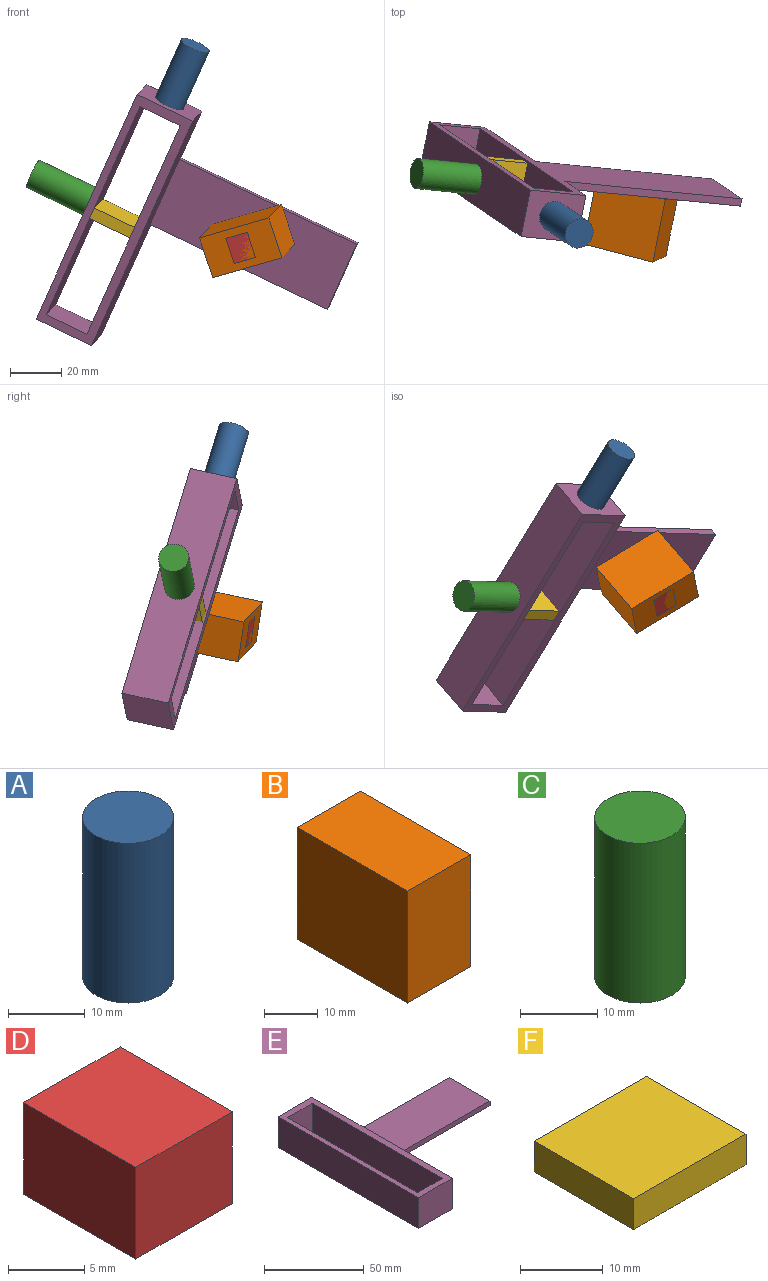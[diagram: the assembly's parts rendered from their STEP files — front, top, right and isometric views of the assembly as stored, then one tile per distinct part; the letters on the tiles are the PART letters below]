
ASSEMBLY  parts=6 mates=5
PART A: 3 faces, bbox 11.8x11.8x25.4 mm
  f0: cylinder r=5.91mm len=25.4mm, axis (0,0,-1), area 942.4mm2, adj f1,f2
  f1: plane 11.81x11.81mm, normal (0,0,1), area 109.5mm2, adj f0
  f2: plane 11.81x11.81mm, normal (0,0,-1), area 109.5mm2, adj f0
PART B: 6 faces, bbox 16.5x28.9x25.4 mm
  f0: plane 28.93x25.4mm, normal (1,0,0), area 734.7mm2, adj f1,f3,f4,f5
  f1: plane 25.4x16.52mm, normal (0,1,0), area 419.6mm2, adj f0,f2,f4,f5
  f2: plane 28.93x25.4mm, normal (-1,0,0), area 734.7mm2, adj f1,f3,f4,f5
  f3: plane 25.4x16.52mm, normal (0,-1,0), area 419.6mm2, adj f0,f2,f4,f5
  f4: plane 28.93x16.52mm, normal (0,0,1), area 477.8mm2, adj f0,f1,f2,f3
  f5: plane 28.93x16.52mm, normal (0,0,-1), area 477.8mm2, adj f0,f1,f2,f3
PART C: 3 faces, bbox 11.8x11.8x25.4 mm
  f0: cylinder r=5.88mm len=25.4mm, axis (0,0,-1), area 939mm2, adj f1,f2
  f1: plane 11.77x11.77mm, normal (0,0,1), area 108.8mm2, adj f0
  f2: plane 11.77x11.77mm, normal (0,0,-1), area 108.8mm2, adj f0
PART D: 6 faces, bbox 9x10.4x7.4 mm
  f0: plane 8.96x7.39mm, normal (0,-1,0), area 66.2mm2, adj f1,f3,f4,f5
  f1: plane 10.43x7.39mm, normal (1,0,0), area 77.1mm2, adj f0,f2,f4,f5
  f2: plane 8.96x7.39mm, normal (0,1,0), area 66.2mm2, adj f1,f3,f4,f5
  f3: plane 10.43x7.39mm, normal (-1,0,0), area 77.1mm2, adj f0,f2,f4,f5
  f4: plane 10.43x8.96mm, normal (0,0,1), area 93.4mm2, adj f0,f1,f2,f3
  f5: plane 10.43x8.96mm, normal (0,0,-1), area 93.4mm2, adj f0,f1,f2,f3
PART E: 14 faces, bbox 100.8x99.5x18.8 mm
  f0: plane 24.05x18.84mm, normal (0,1,0), area 453.1mm2, adj f1,f7,f8,f9
  f1: plane 99.49x18.84mm, normal (-1,0,0), area 1874.5mm2, adj f0,f2,f8,f9
  f2: plane 24.05x18.84mm, normal (0,-1,0), area 453.1mm2, adj f1,f7,f8,f9
  f3: plane 92.25x18.84mm, normal (1,0,0), area 1738.2mm2, adj f4,f6,f8,f9
  f4: plane 18.84x17.52mm, normal (0,-1,0), area 330.1mm2, adj f3,f5,f8,f9
  f5: plane 92.25x18.84mm, normal (-1,0,0), area 1738.2mm2, adj f4,f6,f8,f9
  f6: plane 18.84x17.52mm, normal (0,1,0), area 330.1mm2, adj f3,f5,f8,f9
  f7: plane 99.49x18.84mm, normal (1,0,0), area 1789.2mm2, adj f0,f2,f8,f9,f10,f11,f12
  f8: plane 99.49x24.05mm, normal (0,0,1), area 776.5mm2, adj f0,f1,f2,f3,f4,f5,f6,f7
  f9: plane 100.79x99.49mm, normal (0,0,-1), area 2996.4mm2, adj f0,f1,f2,f3,f4,f5,f6,f7
  f10: plane 76.74x28.93mm, normal (0,0,1), area 2219.9mm2, adj f7,f11,f12,f13
  f11: plane 76.74x2.95mm, normal (0,1,0), area 226.5mm2, adj f7,f9,f10,f13
  f12: plane 76.74x2.95mm, normal (0,-1,0), area 226.5mm2, adj f7,f9,f10,f13
  f13: plane 28.93x2.95mm, normal (1,0,0), area 85.4mm2, adj f9,f10,f11,f12
PART F: 6 faces, bbox 19.2x17.1x4.6 mm
  f0: plane 19.21x4.57mm, normal (0,-1,0), area 87.8mm2, adj f1,f3,f4,f5
  f1: plane 17.12x4.57mm, normal (1,0,0), area 78.3mm2, adj f0,f2,f4,f5
  f2: plane 19.21x4.57mm, normal (0,1,0), area 87.8mm2, adj f1,f3,f4,f5
  f3: plane 17.12x4.57mm, normal (-1,0,0), area 78.3mm2, adj f0,f2,f4,f5
  f4: plane 19.21x17.12mm, normal (0,0,1), area 328.8mm2, adj f0,f1,f2,f3
  f5: plane 19.21x17.12mm, normal (0,0,-1), area 328.8mm2, adj f0,f1,f2,f3
PLACE A rot(axis=(0.42,0.22,0.88),62.6deg) t=(-30.29,9.36,-2.73)mm
PLACE B rot(axis=(0.45,-0.73,0.51),129.4deg) t=(3.27,-12.05,-1.21)mm
PLACE C rot(axis=(-0.54,-0.13,0.83),148.1deg) t=(-82.5,-6.46,-87.07)mm
PLACE D rot(axis=(-0.03,0.64,0.77),158.9deg) t=(2.59,-38.08,-2.65)mm
PLACE E rot(axis=(0.96,0.12,-0.25),106.8deg) t=(-2.32,6.05,-80.06)mm
PLACE F rot(axis=(0.48,0.83,-0.28),29.8deg) t=(-43.21,42.6,-47.87)mm
MATE slider E.f2 <-> F.f5  axis (-0.39,0.27,-0.88) through (-70.94,16.42,-95.54)mm
MATE revolute C.f0 <-> E.f1  axis (0.9,-0.09,-0.43) through (-62.1,4.12,-46.65)mm
MATE revolute E.f0 <-> A.f0  axis (0.39,-0.27,0.88) through (-31.66,-10.29,-8.12)mm
MATE fastened B.f4 <-> D.f5  axis (-0.19,-0.96,-0.21) through (-3.9,-23.45,-64.58)mm
MATE revolute E.f10 <-> B.f5  axis (-0.19,-0.96,-0.21) through (0.99,0.92,-59.33)mm
